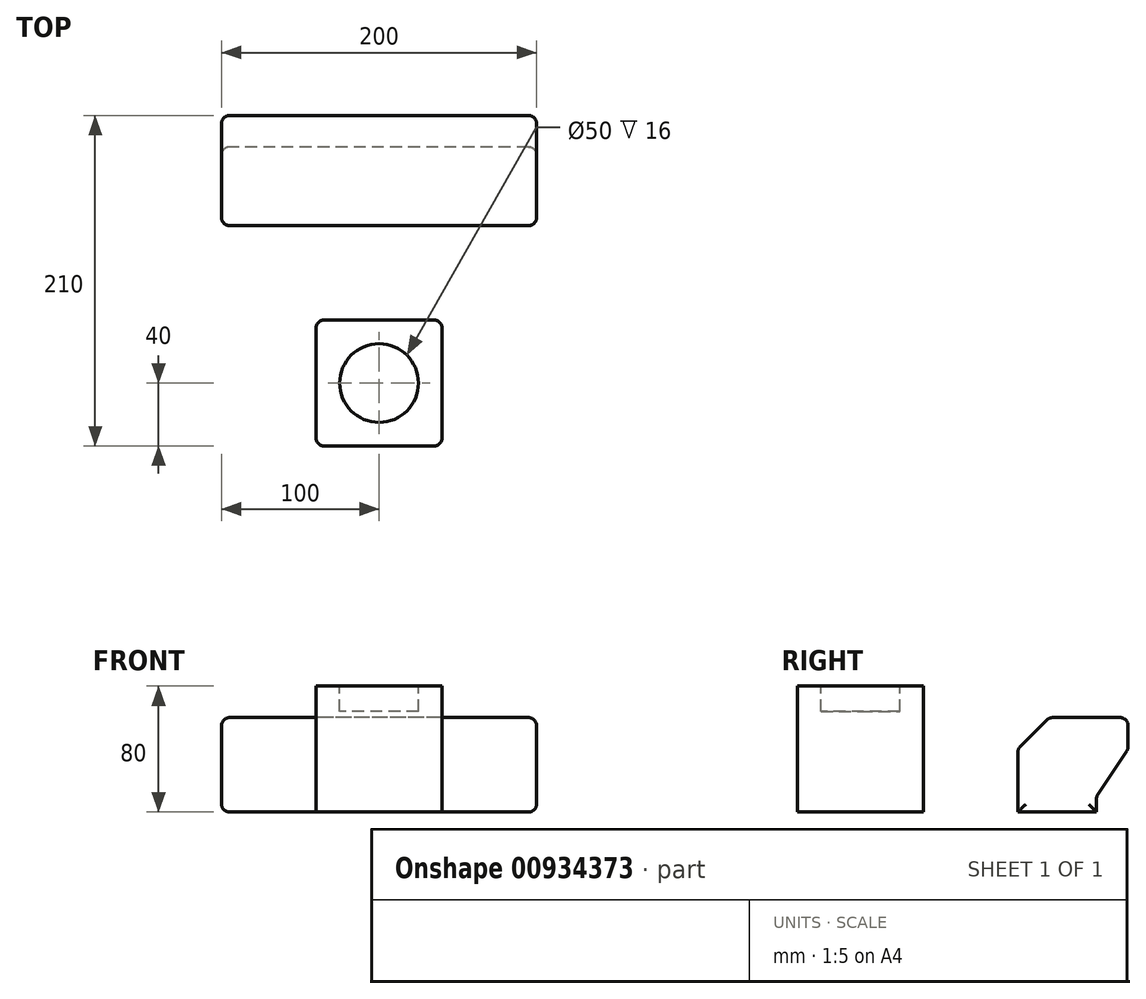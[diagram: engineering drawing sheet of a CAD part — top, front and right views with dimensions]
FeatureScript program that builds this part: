
annotation { "Feature Type Name" : "Feature", "Feature Type Description" : "" }
export const myFeature = defineFeature(function(context is Context, id is Id, definition is map)
    precondition{}
    {
        {
            var Q0;
            Q0=qCreatedBy(makeId("Top.planeOp"),FACE);
            var sketch = newSketch(context, id + "F0", { "sketchPlane" : qUnion([Q0])});
            skLineSegment(sketch, "E0.bottom", {"start": v(40, 40) * mm, "end": v(-40, 40) * mm});
            skLineSegment(sketch, "E0.top", {"start": v(40, -40) * mm, "end": v(-40, -40) * mm});
            skLineSegment(sketch, "E0.left", {"start": v(40, 40) * mm, "end": v(40, -40) * mm});
            skLineSegment(sketch, "E0.right", {"start": v(-40, 40) * mm, "end": v(-40, -40) * mm});
            skPoint(sketch, "E0.middle", {"position": v(0, 0) * mm});
            skSolve(sketch);
        }
        {
            var Q0;
            Q0 = qSketchRegion(id + "F0", true);
            extrude(context, id + "F1", {"entities" : qUnion([Q0]), "depth" : 80 * mm, "offsetDistance" : 25 * mm});
        }
        {
            var Q0;
            Q0=makeQuery(id+"F1.opExtrude","CAP_FACE",FACE,{"disambiguationData":[OSD([sQuery(id+"F0.wireOp",EDGE,"E0.bottom"),sQuery(id+"F0.wireOp",EDGE,"E0.top"),sQuery(id+"F0.wireOp",EDGE,"E0.left"),sQuery(id+"F0.wireOp",EDGE,"E0.right")])],"isStart":false});
            var sketch = newSketch(context, id + "F2", { "sketchPlane" : qUnion([Q0])});
            skCircle(sketch, "E1", {"center": v(0, 0) * mm, "radius": 25 * mm});
            skSolve(sketch);
        }
        {
            var Q0;
            Q0 = qSketchRegion(id + "F2", true);
            extrude(context, id + "F3", {"entities" : qUnion([Q0]), "operationType" : NewBodyOperationType.REMOVE, "oppositeDirection" : true, "depth" : 16 * mm, "offsetDistance" : 25 * mm});
        }
        {
            var Q0;
            Q0=makeQuery(id+"F1.opExtrude","SWEPT_EDGE",EDGE,{"disambiguationData":[OSD([sQuery(id+"F0.wireOp",EDGE,"E0.top"),sQuery(id+"F0.wireOp",EDGE,"E0.right")])]});
            var Q1;
            Q1=makeQuery(id+"F1.opExtrude","SWEPT_EDGE",EDGE,{"disambiguationData":[OSD([sQuery(id+"F0.wireOp",EDGE,"E0.bottom"),sQuery(id+"F0.wireOp",EDGE,"E0.right")])]});
            var Q2;
            Q2=makeQuery(id+"F1.opExtrude","SWEPT_EDGE",EDGE,{"disambiguationData":[OSD([sQuery(id+"F0.wireOp",EDGE,"E0.bottom"),sQuery(id+"F0.wireOp",EDGE,"E0.left")])]});
            var Q3;
            Q3=makeQuery(id+"F1.opExtrude","SWEPT_EDGE",EDGE,{"disambiguationData":[OSD([sQuery(id+"F0.wireOp",EDGE,"E0.top"),sQuery(id+"F0.wireOp",EDGE,"E0.left")])]});
            fillet(context, id + "F4", {"entities" : qUnion([Q0, Q1, Q2, Q3]), "radius" : 5 * mm, "tangentPropagation" : true, "allowEdgeOverflow" : false});
        }
        {
            var Q0;
            Q0=qCreatedBy(makeId("Right.planeOp"),FACE);
            var sketch = newSketch(context, id + "F5", { "sketchPlane" : qUnion([Q0])});
            skLineSegment(sketch, "E2", {"start": v(100, 0) * mm, "end": v(150, 0) * mm});
            skLineSegment(sketch, "E3", {"start": v(150, 0) * mm, "end": v(150, 10) * mm});
            skLineSegment(sketch, "E4", {"start": v(150, 10) * mm, "end": v(170, 40) * mm});
            skLineSegment(sketch, "E5", {"start": v(170, 40) * mm, "end": v(170, 60) * mm});
            skLineSegment(sketch, "E6", {"start": v(170, 60) * mm, "end": v(120, 60) * mm});
            skLineSegment(sketch, "E7", {"start": v(120, 60) * mm, "end": v(100, 40) * mm});
            skLineSegment(sketch, "E8", {"start": v(100, 40) * mm, "end": v(100, 0) * mm});
            skSolve(sketch);
        }
        {
            var Q0;
            Q0 = qSketchRegion(id + "F5", true);
            extrude(context, id + "F6", {"entities" : qUnion([Q0]), "depth" : 100 * mm, "offsetDistance" : 25 * mm, "hasSecondDirection" : true, "secondDirectionOppositeDirection" : true, "secondDirectionDepth" : 100 * mm});
        }
        {
            var Q0;
            Q0=makeQuery(id+"F6.opExtrude","SWEPT_EDGE",EDGE,{"disambiguationData":[OSD([sQuery(id+"F5.wireOp",EDGE,"E7"),sQuery(id+"F5.wireOp",EDGE,"E8")])]});
            var Q1;
            Q1=makeQuery(id+"F6.opExtrude","SWEPT_EDGE",EDGE,{"disambiguationData":[OSD([sQuery(id+"F5.wireOp",EDGE,"E6"),sQuery(id+"F5.wireOp",EDGE,"E7")])]});
            var Q2;
            Q2=makeQuery(id+"F6.opExtrude","SWEPT_EDGE",EDGE,{"disambiguationData":[OSD([sQuery(id+"F5.wireOp",EDGE,"E5"),sQuery(id+"F5.wireOp",EDGE,"E6")])]});
            var Q3;
            Q3=makeQuery(id+"F6.opExtrude","SWEPT_EDGE",EDGE,{"disambiguationData":[OSD([sQuery(id+"F5.wireOp",EDGE,"E4"),sQuery(id+"F5.wireOp",EDGE,"E5")])]});
            var Q4;
            Q4=makeQuery(id+"F6.opExtrude","SWEPT_EDGE",EDGE,{"disambiguationData":[OSD([sQuery(id+"F5.wireOp",EDGE,"E3"),sQuery(id+"F5.wireOp",EDGE,"E4")])]});
            var Q5;
            Q5=makeQuery(id+"F6.opExtrude","CAP_FACE",FACE,{"disambiguationData":[OSD([sQuery(id+"F5.wireOp",EDGE,"E2"),sQuery(id+"F5.wireOp",EDGE,"E3"),sQuery(id+"F5.wireOp",EDGE,"E4"),sQuery(id+"F5.wireOp",EDGE,"E5"),sQuery(id+"F5.wireOp",EDGE,"E6"),sQuery(id+"F5.wireOp",EDGE,"E7"),sQuery(id+"F5.wireOp",EDGE,"E8")])],"isStart":false});
            var Q6;
            Q6=makeQuery(id+"F6.opExtrude","CAP_FACE",FACE,{"disambiguationData":[OSD([sQuery(id+"F5.wireOp",EDGE,"E2"),sQuery(id+"F5.wireOp",EDGE,"E3"),sQuery(id+"F5.wireOp",EDGE,"E4"),sQuery(id+"F5.wireOp",EDGE,"E5"),sQuery(id+"F5.wireOp",EDGE,"E6"),sQuery(id+"F5.wireOp",EDGE,"E7"),sQuery(id+"F5.wireOp",EDGE,"E8")])],"isStart":true});
            fillet(context, id + "F7", {"entities" : qUnion([Q0, Q1, Q2, Q3, Q4, Q5, Q6]), "radius" : 5 * mm, "tangentPropagation" : true, "allowEdgeOverflow" : false});
        }
    });
